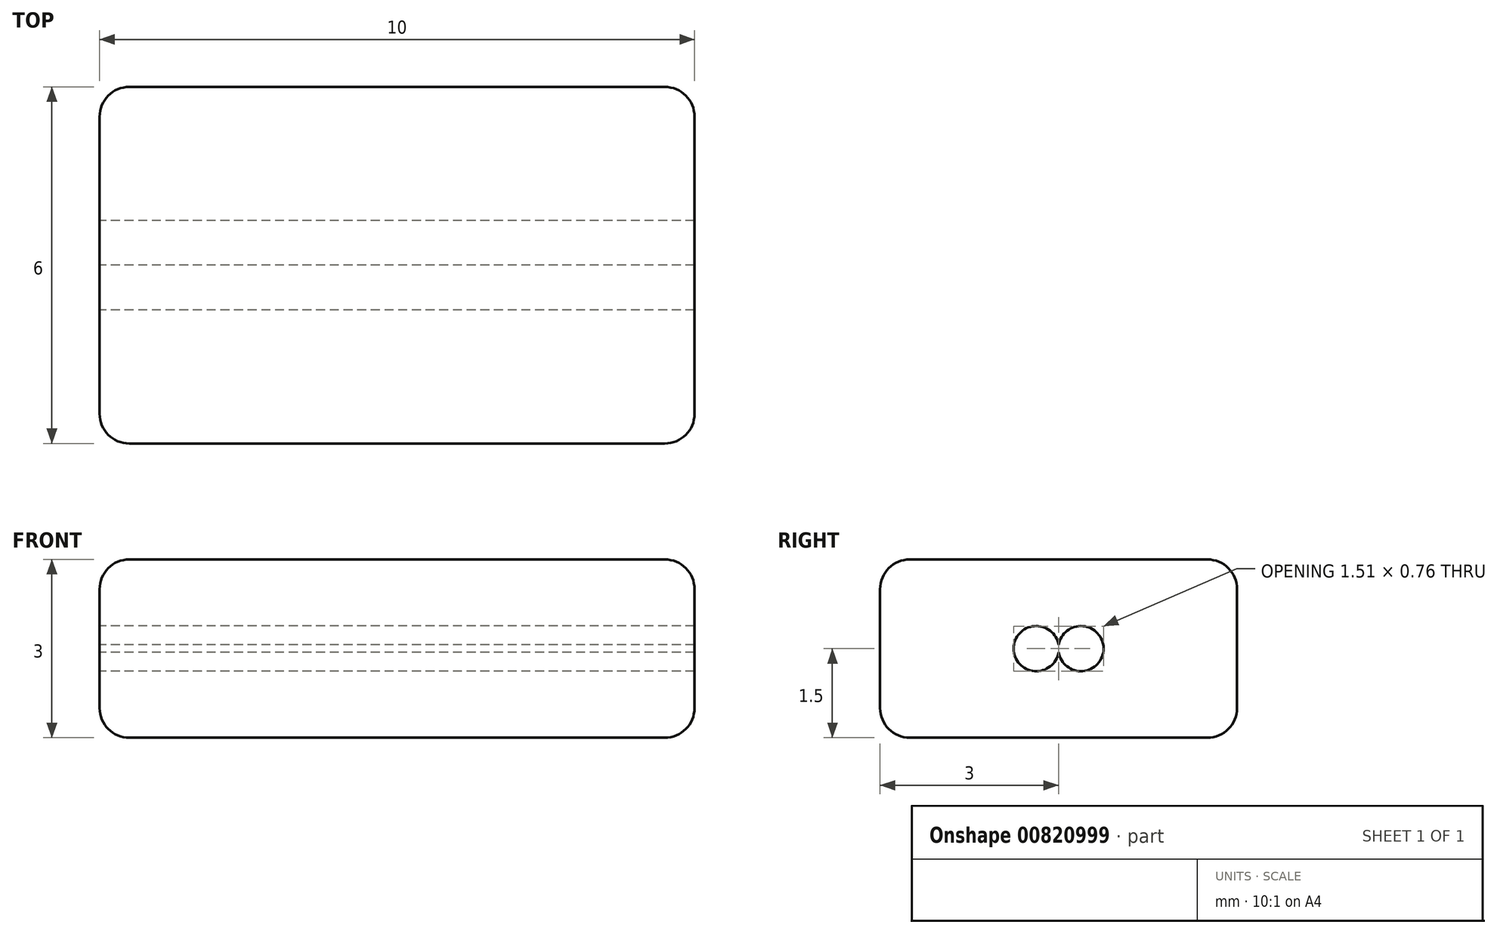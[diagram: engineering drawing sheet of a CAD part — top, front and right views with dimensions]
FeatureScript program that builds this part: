
annotation { "Feature Type Name" : "Feature", "Feature Type Description" : "" }
export const myFeature = defineFeature(function(context is Context, id is Id, definition is map)
    precondition{}
    {
        {
            var Q0;
            Q0=qCreatedBy(makeId("Top.planeOp"),FACE);
            var sketch = newSketch(context, id + "F0", { "sketchPlane" : qUnion([Q0])});
            skLineSegment(sketch, "E0.bottom", {"start": v(-4.5, -3) * mm, "end": v(4.5, -3) * mm});
            skLineSegment(sketch, "E0.top", {"start": v(-4.5, 3) * mm, "end": v(4.5, 3) * mm});
            skLineSegment(sketch, "E0.left", {"start": v(-5, -2.5) * mm, "end": v(-5, 2.5) * mm});
            skLineSegment(sketch, "E0.right", {"start": v(5, -2.5) * mm, "end": v(5, 2.5) * mm});
            skPoint(sketch, "E0.middle", {"position": v(0, 0) * mm});
            skPoint(sketch, "E1.visualSharp", {"position": v(-5, 3) * mm});
            skArc(sketch, "E1.filletArc", {"start": v(-4.5, 3) * mm, "mid": v(-4.85, 2.85) * mm, "end": v(-5, 2.5) * mm});
            skPoint(sketch, "E2.visualSharp", {"position": v(-5, -3) * mm});
            skArc(sketch, "E2.filletArc", {"start": v(-5, -2.5) * mm, "mid": v(-4.85, -2.85) * mm, "end": v(-4.5, -3) * mm});
            skPoint(sketch, "E3.visualSharp", {"position": v(5, -3) * mm});
            skArc(sketch, "E3.filletArc", {"start": v(4.5, -3) * mm, "mid": v(4.85, -2.85) * mm, "end": v(5, -2.5) * mm});
            skPoint(sketch, "E4.visualSharp", {"position": v(5, 3) * mm});
            skArc(sketch, "E4.filletArc", {"start": v(5, 2.5) * mm, "mid": v(4.85, 2.85) * mm, "end": v(4.5, 3) * mm});
            skSolve(sketch);
        }
        {
            var Q0;
            Q0 = qSketchRegion(id + "F0", true);
            extrude(context, id + "F1", {"entities" : qUnion([Q0]), "endBound" : BoundingType.SYMMETRIC, "depth" : 3 * mm, "offsetDistance" : 25 * mm});
        }
        {
            var Q0;
            Q0=makeQuery(id+"F1.opExtrude","CAP_EDGE",EDGE,{"disambiguationData":[OSD([sQuery(id+"F0.wireOp",EDGE,"E0.top")])],"isStart":false});
            var Q1;
            Q1=makeQuery(id+"F1.opExtrude","CAP_EDGE",EDGE,{"disambiguationData":[OSD([sQuery(id+"F0.wireOp",EDGE,"E0.left")])],"isStart":true});
            fillet(context, id + "F2", {"entities" : qUnion([Q0, Q1]), "radius" : .5 * mm, "tangentPropagation" : true, "allowEdgeOverflow" : false});
        }
        {
            var Q0;
            Q0=qCreatedBy(makeId("Right.planeOp"),FACE);
            var sketch = newSketch(context, id + "F3", { "sketchPlane" : qUnion([Q0])});
            skCircle(sketch, "E5", {"center": v(-0.38, 0) * mm, "radius": 0.38 * mm});
            skCircle(sketch, "E6", {"center": v(0.37, 0) * mm, "radius": 0.38 * mm});
            skSolve(sketch);
        }
        {
            var Q0;
            Q0 = qSketchRegion(id + "F3", true);
            extrude(context, id + "F4", {"entities" : qUnion([Q0]), "operationType" : NewBodyOperationType.REMOVE, "endBound" : BoundingType.SYMMETRIC, "depth" : 30 * mm, "offsetDistance" : 25 * mm});
        }
    });
